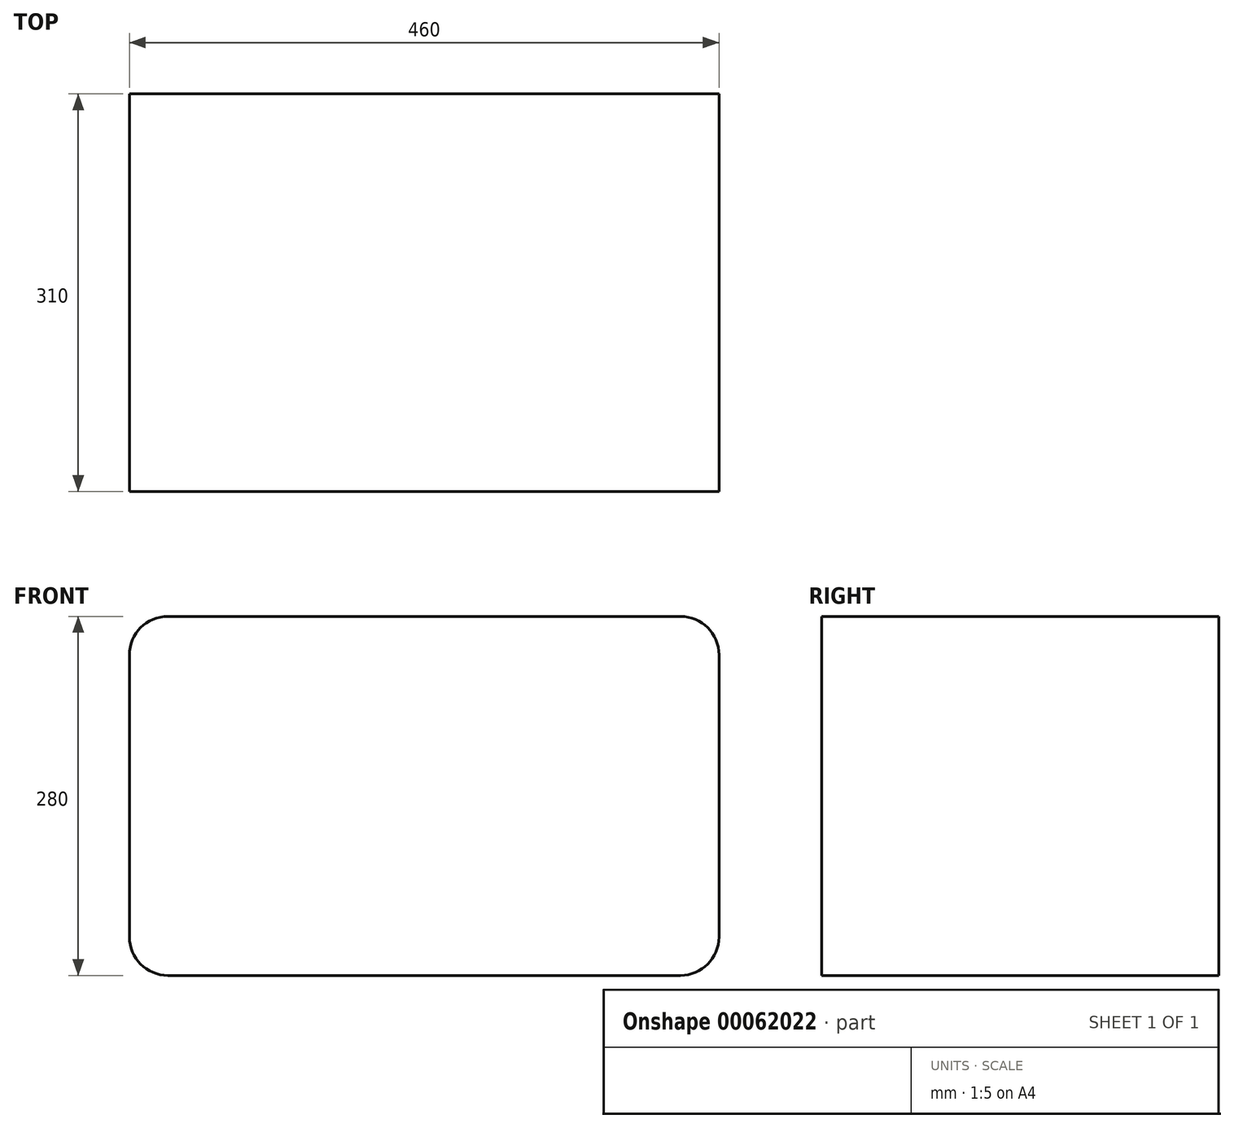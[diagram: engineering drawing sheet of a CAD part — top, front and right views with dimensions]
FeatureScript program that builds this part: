
annotation { "Feature Type Name" : "Feature", "Feature Type Description" : "" }
export const myFeature = defineFeature(function(context is Context, id is Id, definition is map)
    precondition{}
    {
        {
            var Q0;
            Q0=qCreatedBy(makeId("Front.planeOp"),FACE);
            var sketch = newSketch(context, id + "F0", { "sketchPlane" : qUnion([Q0])});
            skLineSegment(sketch, "E0.bottom", {"start": v(0, 0) * mm, "end": v(460, 0) * mm});
            skLineSegment(sketch, "E0.top", {"start": v(0, 280) * mm, "end": v(460, 280) * mm});
            skLineSegment(sketch, "E0.left", {"start": v(0, 0) * mm, "end": v(0, 280) * mm});
            skLineSegment(sketch, "E0.right", {"start": v(460, 0) * mm, "end": v(460, 280) * mm});
            skSolve(sketch);
        }
        {
            var Q0;
            Q0=makeQuery(id+"F0.imprint","IMPRINT",FACE,{"disambiguationData":[TD([[makeQuery(id+"F0.imprint","IMPRINT",EDGE,{"derivedFrom":sQuery(id+"F0.wireOp",EDGE,"E0.bottom")}),1.0]])]});
            extrude(context, id + "F1", {"entities" : qUnion([Q0]), "depth" : 310 * mm});
        }
        {
            var Q0;
            Q0=makeQuery(id+"F1.opExtrude","SWEPT_EDGE",EDGE,{"disambiguationData":[OSD([sQuery(id+"F0.wireOp",EDGE,"E0.top"),sQuery(id+"F0.wireOp",EDGE,"E0.right")])]});
            var Q1;
            Q1=makeQuery(id+"F1.opExtrude","SWEPT_EDGE",EDGE,{"disambiguationData":[OSD([sQuery(id+"F0.wireOp",EDGE,"E0.top"),sQuery(id+"F0.wireOp",EDGE,"E0.left")])]});
            var Q2;
            Q2=makeQuery(id+"F1.opExtrude","SWEPT_EDGE",EDGE,{"disambiguationData":[OSD([sQuery(id+"F0.wireOp",EDGE,"E0.bottom"),sQuery(id+"F0.wireOp",EDGE,"E0.right")])]});
            var Q3;
            Q3=makeQuery(id+"F1.opExtrude","SWEPT_EDGE",EDGE,{"disambiguationData":[OSD([sQuery(id+"F0.wireOp",EDGE,"E0.bottom"),sQuery(id+"F0.wireOp",EDGE,"E0.left")])]});
            fillet(context, id + "F2", {"entities" : qUnion([Q0, Q1, Q2, Q3]), "radius" : 30 * mm, "tangentPropagation" : true, "allowEdgeOverflow" : false});
        }
    });
